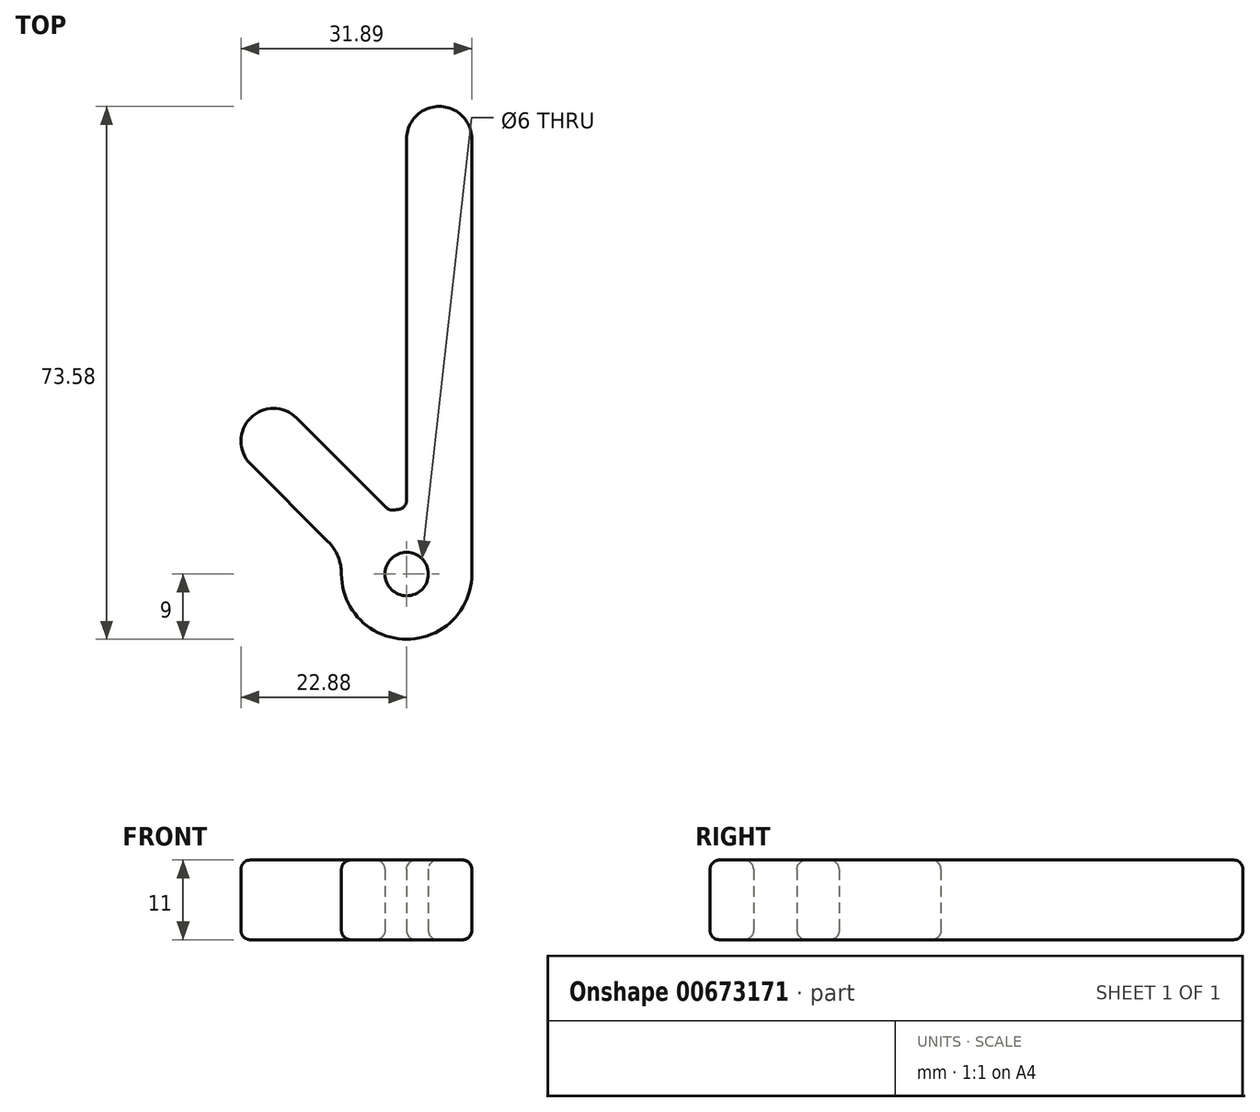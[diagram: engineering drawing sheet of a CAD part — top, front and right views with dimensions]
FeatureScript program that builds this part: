
annotation { "Feature Type Name" : "Feature", "Feature Type Description" : "" }
export const myFeature = defineFeature(function(context is Context, id is Id, definition is map)
    precondition{}
    {
        {
            var Q0;
            Q0=qCreatedBy(makeId("Top.planeOp"),FACE);
            var sketch = newSketch(context, id + "F0", { "sketchPlane" : qUnion([Q0])});
            skCircle(sketch, "E0", {"center": v(0, 0) * mm, "radius": 3 * mm});
            skArc(sketch, "E1.0", {"start": v(-9, 0) * mm, "mid": v(0, -9) * mm, "end": v(9, 0) * mm});
            skLineSegment(sketch, "E2", {"start": v(0, 9) * mm, "end": v(0, 59.8) * mm});
            skLineSegment(sketch, "E3", {"start": v(9, 0) * mm, "end": v(9, 59.8) * mm});
            skArc(sketch, "E4", {"start": v(9, 59.8) * mm, "mid": v(4.5, 64.58) * mm, "end": v(0, 59.8) * mm});
            skPoint(sketch, "E4.third.point", {"position": v(4.69, 55.57) * mm});
            skPoint(sketch, "E5.end.orphan", {"position": v(7.1, 59.8) * mm});
            skLineSegment(sketch, "E6", {"start": v(-15.2, 21.57) * mm, "end": v(-2.33, 8.7) * mm});
            skLineSegment(sketch, "E7", {"start": v(-21.57, 15.2) * mm, "end": v(-10.86, 4.5) * mm});
            skArc(sketch, "E8.trimOffspring", {"start": v(0, 9) * mm, "mid": v(-1.17, 8.92) * mm, "end": v(-2.33, 8.7) * mm});
            skPoint(sketch, "E9.visualSharp", {"position": v(-8.7, 2.33) * mm});
            skArc(sketch, "E9.filletArc", {"start": v(-9, 0) * mm, "mid": v(-9.48, 2.43) * mm, "end": v(-10.86, 4.5) * mm});
            skArc(sketch, "E10", {"start": v(-15.2, 21.57) * mm, "mid": v(-21.57, 21.57) * mm, "end": v(-21.57, 15.2) * mm});
            skPoint(sketch, "E10.third.point", {"position": v(-21.57, 21.57) * mm});
            skPoint(sketch, "E11.start.orphan", {"position": v(-9, 0) * mm});
            skPoint(sketch, "E12.end.orphan", {"position": v(-59.8, 59.8) * mm});
            skSolve(sketch);
        }
        {
            var Q0;
            Q0=makeQuery(id+"F0.imprint","IMPRINT",FACE,{"disambiguationData":[TD([[makeQuery(id+"F0.imprint","IMPRINT",EDGE,{"derivedFrom":sQuery(id+"F0.wireOp",EDGE,"E0")}),-1.0]])]});
            extrude(context, id + "F1", {"entities" : qUnion([Q0]), "depth" : 11 * mm, "offsetDistance" : 25.4 * mm});
        }
        {
            var Q0;
            Q0=makeQuery(id+"F1.opExtrude","CAP_EDGE",EDGE,{"disambiguationData":[OSD([sQuery(id+"F0.wireOp",EDGE,"E1.0")])],"isStart":false});
            var Q1;
            Q1=makeQuery(id+"F1.opExtrude","CAP_EDGE",EDGE,{"disambiguationData":[OSD([sQuery(id+"F0.wireOp",EDGE,"E1.0")])],"isStart":true});
            var Q2;
            Q2=makeQuery(id+"F1.opExtrude","SWEPT_FACE",FACE,{"disambiguationData":[OSD([sQuery(id+"F0.wireOp",EDGE,"E9.filletArc")])]});
            var Q3;
            Q3=makeQuery(id+"F1.opExtrude","SWEPT_FACE",FACE,{"disambiguationData":[OSD([sQuery(id+"F0.wireOp",EDGE,"E7")])]});
            var Q4;
            Q4=makeQuery(id+"F1.opExtrude","SWEPT_FACE",FACE,{"disambiguationData":[OSD([sQuery(id+"F0.wireOp",EDGE,"E10")])]});
            var Q5;
            Q5=makeQuery(id+"F1.opExtrude","SWEPT_FACE",FACE,{"disambiguationData":[OSD([sQuery(id+"F0.wireOp",EDGE,"E6")])]});
            var Q6;
            Q6=makeQuery(id+"F1.opExtrude","SWEPT_EDGE",EDGE,{"disambiguationData":[OSD([sQuery(id+"F0.wireOp",EDGE,"E2"),sQuery(id+"F0.wireOp",EDGE,"E8.trimOffspring")])]});
            var Q7;
            Q7=makeQuery(id+"F1.opExtrude","SWEPT_FACE",FACE,{"disambiguationData":[OSD([sQuery(id+"F0.wireOp",EDGE,"E2")])]});
            var Q8;
            Q8=makeQuery(id+"F1.opExtrude","CAP_FACE",FACE,{"disambiguationData":[OSD([sQuery(id+"F0.wireOp",EDGE,"E0"),sQuery(id+"F0.wireOp",EDGE,"E1.0"),sQuery(id+"F0.wireOp",EDGE,"E2"),sQuery(id+"F0.wireOp",EDGE,"E3"),sQuery(id+"F0.wireOp",EDGE,"E4"),sQuery(id+"F0.wireOp",EDGE,"E6"),sQuery(id+"F0.wireOp",EDGE,"E7"),sQuery(id+"F0.wireOp",EDGE,"E8.trimOffspring"),sQuery(id+"F0.wireOp",EDGE,"E9.filletArc"),sQuery(id+"F0.wireOp",EDGE,"E10")])],"isStart":false});
            var Q9;
            Q9=makeQuery(id+"F1.opExtrude","SWEPT_FACE",FACE,{"disambiguationData":[OSD([sQuery(id+"F0.wireOp",EDGE,"E3")])]});
            var Q10;
            Q10=makeQuery(id+"F1.opExtrude","SWEPT_FACE",FACE,{"disambiguationData":[OSD([sQuery(id+"F0.wireOp",EDGE,"E4")])]});
            var Q11;
            Q11=makeQuery(id+"F1.opExtrude","CAP_FACE",FACE,{"disambiguationData":[OSD([sQuery(id+"F0.wireOp",EDGE,"E0"),sQuery(id+"F0.wireOp",EDGE,"E1.0"),sQuery(id+"F0.wireOp",EDGE,"E2"),sQuery(id+"F0.wireOp",EDGE,"E3"),sQuery(id+"F0.wireOp",EDGE,"E4"),sQuery(id+"F0.wireOp",EDGE,"E6"),sQuery(id+"F0.wireOp",EDGE,"E7"),sQuery(id+"F0.wireOp",EDGE,"E8.trimOffspring"),sQuery(id+"F0.wireOp",EDGE,"E9.filletArc"),sQuery(id+"F0.wireOp",EDGE,"E10")])],"isStart":true});
            fillet(context, id + "F2", {"entities" : qUnion([Q0, Q1, Q2, Q3, Q4, Q5, Q6, Q7, Q8, Q9, Q10, Q11]), "radius" : 1.27 * mm, "tangentPropagation" : true, "allowEdgeOverflow" : false});
        }
    });
